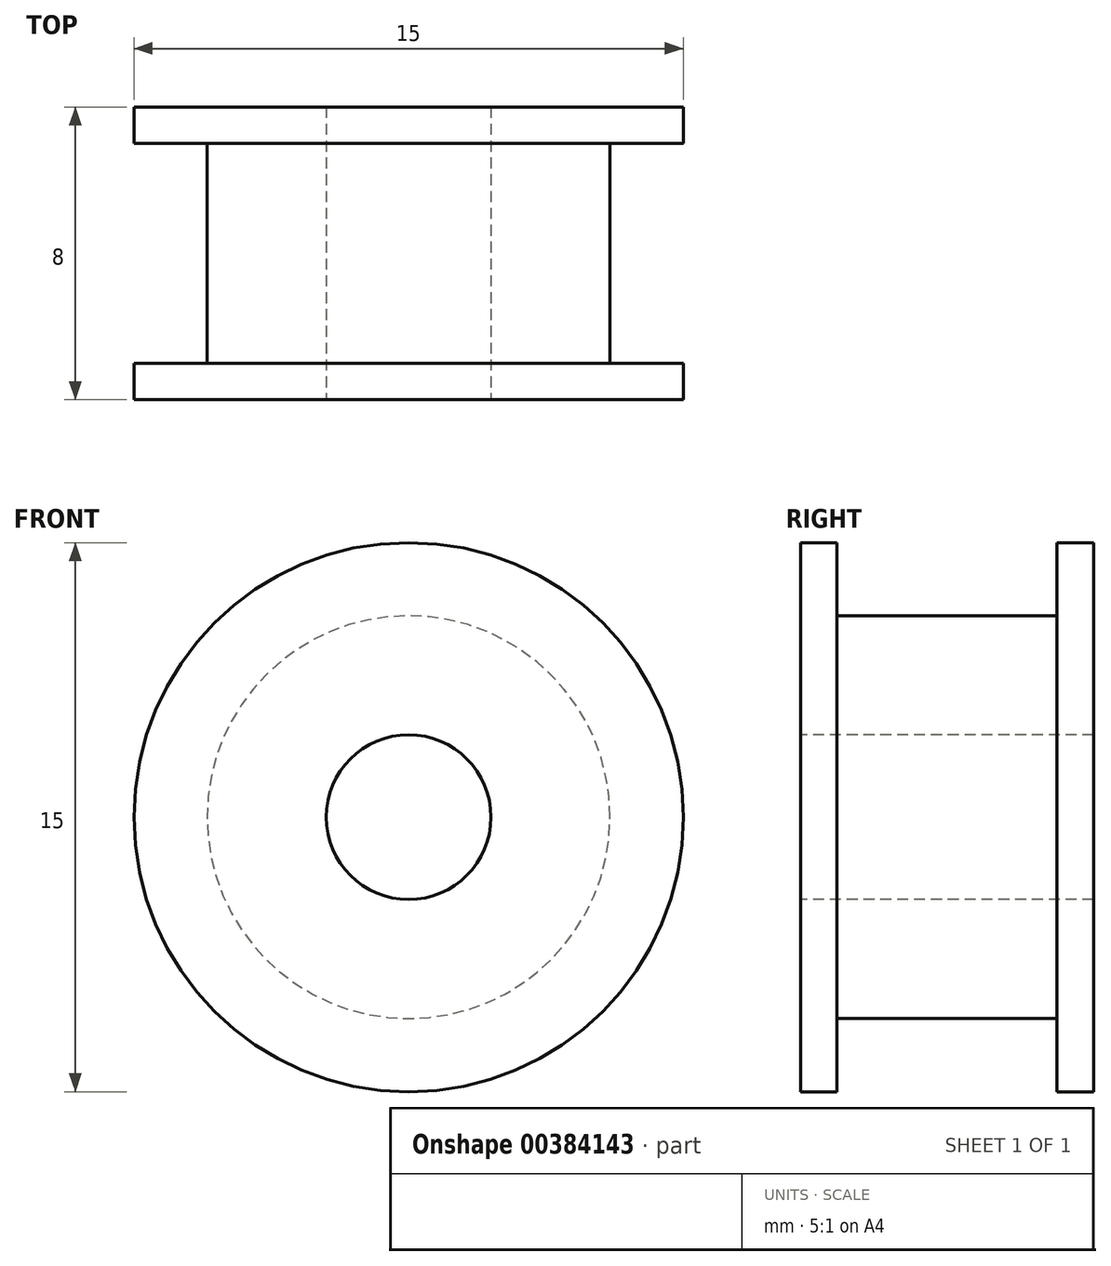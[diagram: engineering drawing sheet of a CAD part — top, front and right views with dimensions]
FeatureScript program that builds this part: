
annotation { "Feature Type Name" : "Feature", "Feature Type Description" : "" }
export const myFeature = defineFeature(function(context is Context, id is Id, definition is map)
    precondition{}
    {
        {
            var Q0;
            Q0=qCreatedBy(makeId("Front.planeOp"),FACE);
            var sketch = newSketch(context, id + "F0", { "sketchPlane" : qUnion([Q0])});
            skCircle(sketch, "E0", {"center": v(0, 0) * mm, "radius": 7.5 * mm});
            skCircle(sketch, "E1", {"center": v(0, 0) * mm, "radius": 2.25 * mm});
            skSolve(sketch);
        }
        {
            var Q0;
            Q0=makeQuery(id+"F0.imprint","IMPRINT",FACE,{"disambiguationData":[TD([[makeQuery(id+"F0.imprint","IMPRINT",EDGE,{"derivedFrom":sQuery(id+"F0.wireOp",EDGE,"E0")}),1.0]])]});
            extrude(context, id + "F1", {"entities" : qUnion([Q0]), "oppositeDirection" : true, "depth" : 1 * mm});
        }
        {
            var Q0;
            Q0=makeQuery(id+"F1.opExtrude","CAP_FACE",FACE,{"disambiguationData":[OSD([sQuery(id+"F0.wireOp",EDGE,"E0"),sQuery(id+"F0.wireOp",EDGE,"E1")])],"isStart":true});
            var sketch = newSketch(context, id + "F2", { "sketchPlane" : qUnion([Q0])});
            skCircle(sketch, "E2", {"center": v(0, 0) * mm, "radius": 5.5 * mm});
            skSolve(sketch);
        }
        {
            var Q0;
            Q0=makeQuery(id+"F2.imprint","IMPRINT",FACE,{"disambiguationData":[TD([[makeQuery(id+"F2.imprint","IMPRINT",EDGE,{"derivedFrom":sQuery(id+"F2.wireOp",EDGE,"E2")}),1.0]])]});
            extrude(context, id + "F3", {"entities" : qUnion([Q0]), "operationType" : NewBodyOperationType.ADD, "depth" : 6 * mm});
        }
        {
            var Q0;
            Q0=makeQuery(id+"F3.opExtrude","CAP_FACE",FACE,{"disambiguationData":[OSD([sQuery(id+"F0.wireOp",EDGE,"E1"),sQuery(id+"F2.wireOp",EDGE,"E2")])],"isStart":false});
            var sketch = newSketch(context, id + "F4", { "sketchPlane" : qUnion([Q0])});
            skCircle(sketch, "E3", {"center": v(0, 0) * mm, "radius": 7.5 * mm});
            skCircle(sketch, "E4", {"center": v(0, 0) * mm, "radius": 2.25 * mm});
            skSolve(sketch);
        }
        {
            var Q0;
            Q0 = qSketchRegion(id + "F4", true);
            extrude(context, id + "F5", {"entities" : qUnion([Q0]), "operationType" : NewBodyOperationType.ADD, "depth" : 1 * mm});
        }
    });
